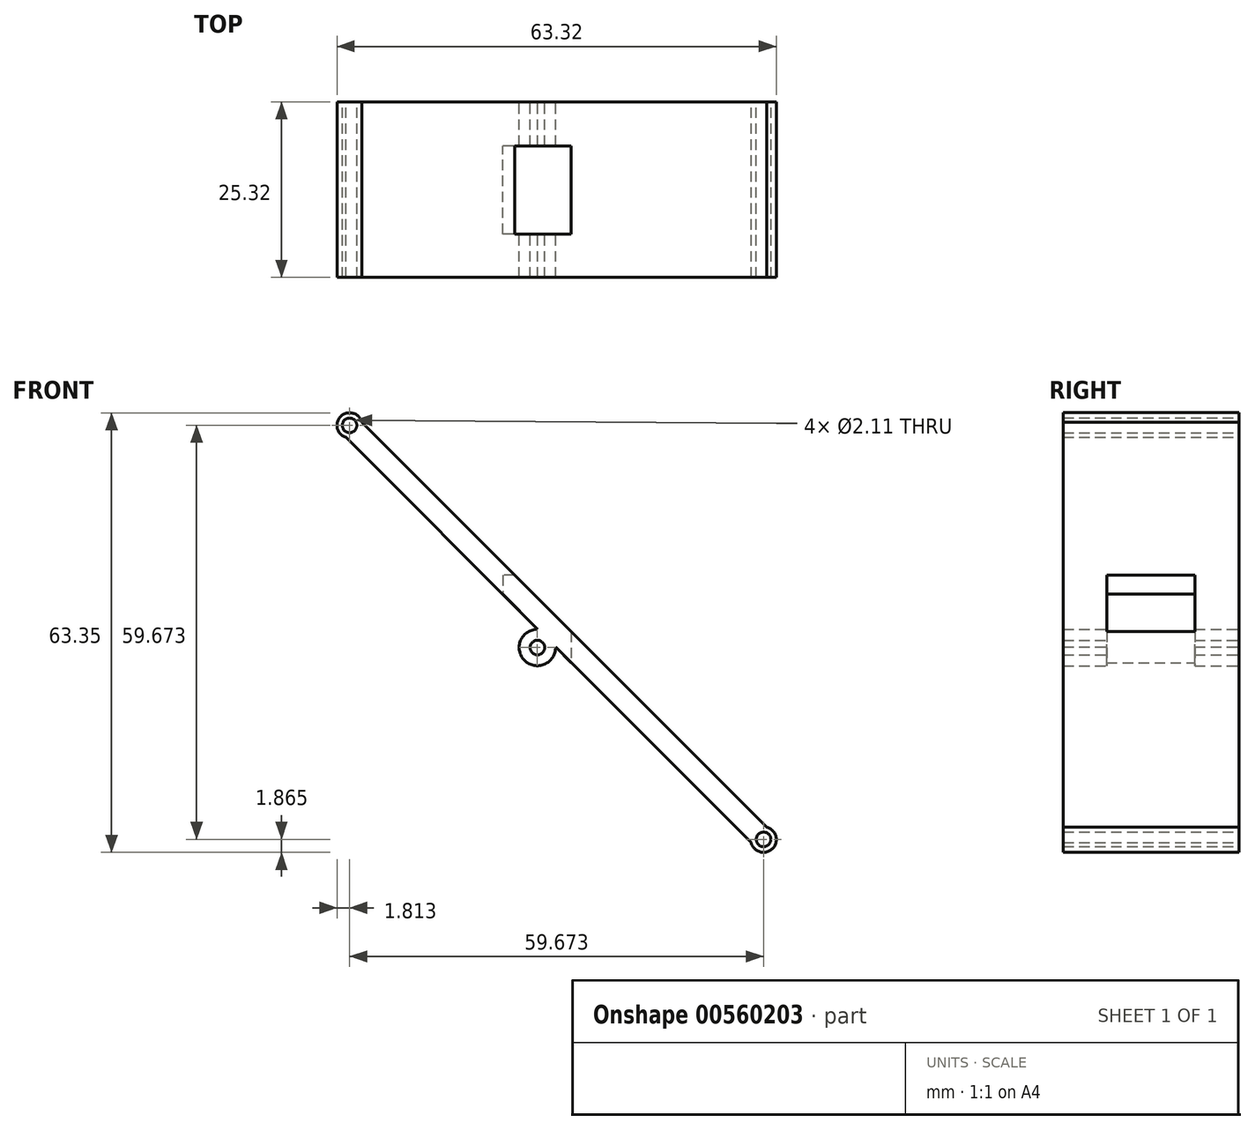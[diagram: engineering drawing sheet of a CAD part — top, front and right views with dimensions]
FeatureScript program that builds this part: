
annotation { "Feature Type Name" : "Feature", "Feature Type Description" : "" }
export const myFeature = defineFeature(function(context is Context, id is Id, definition is map)
    precondition{}
    {
        {
            var Q0;
            Q0=qCreatedBy(makeId("Front.planeOp"),FACE);
            var sketch = newSketch(context, id + "F0", { "sketchPlane" : qUnion([Q0])});
            skLineSegment(sketch, "E0", {"start": v(0, 0) * mm, "end": v(-9.73, 0) * mm, "construction": true});
            skArc(sketch, "E1", {"start": v(-1.78, -0.46) * mm, "mid": v(1.3, -1.3) * mm, "end": v(0.46, 1.78) * mm});
            skLineSegment(sketch, "E2.0", {"start": v(0.46, 1.78) * mm, "end": v(-57.9, 60.15) * mm});
            skLineSegment(sketch, "E3.0", {"start": v(-1.78, -0.46) * mm, "end": v(-29.98, 27.73) * mm});
            skArc(sketch, "E4.MirrorC", {"start": v(-60.2, 57.96) * mm, "mid": v(-60.92, 61.01) * mm, "end": v(-57.9, 60.15) * mm});
            skPoint(sketch, "E5.start.orphan", {"position": v(-30.97, 28.72) * mm});
            skCircle(sketch, "E6.0", {"center": v(-59.67, 59.7) * mm, "radius": 1.05 * mm});
            skCircle(sketch, "E7.MirrorC", {"center": v(0, 0.02) * mm, "radius": 1.05 * mm});
            skPoint(sketch, "E8.orphan", {"position": v(-60.15, 57.9) * mm});
            skArc(sketch, "E9", {"start": v(-32.54, 30.3) * mm, "mid": v(-34.45, 25.82) * mm, "end": v(-29.98, 27.73) * mm});
            skCircle(sketch, "E10.0", {"center": v(-32.6, 27.68) * mm, "radius": 1.05 * mm});
            skLineSegment(sketch, "E11.trimOffspring", {"start": v(-32.54, 30.3) * mm, "end": v(-60.2, 57.96) * mm});
            skSolve(sketch);
        }
        {
            var Q0;
            Q0=makeQuery(id+"F0.imprint","IMPRINT",FACE,{"disambiguationData":[TD([[makeQuery(id+"F0.imprint","IMPRINT",EDGE,{"derivedFrom":sQuery(id+"F0.wireOp",EDGE,"E1")}),1.0]])]});
            extrude(context, id + "F1", {"entities" : qUnion([Q0]), "depth" : 25.32 * mm, "offsetDistance" : 25.4 * mm});
        }
        {
            var Q0;
            Q0=qCreatedBy(makeId("Top.planeOp"),FACE);
            var sketch = newSketch(context, id + "F2", { "sketchPlane" : qUnion([Q0])});
            skLineSegment(sketch, "E12.bottom", {"start": v(-27.7, -19.05) * mm, "end": v(-37.6, -19.05) * mm});
            skLineSegment(sketch, "E12.top", {"start": v(-27.7, -6.35) * mm, "end": v(-37.6, -6.35) * mm});
            skLineSegment(sketch, "E12.left", {"start": v(-27.7, -19.05) * mm, "end": v(-27.7, -6.35) * mm});
            skLineSegment(sketch, "E12.right", {"start": v(-37.6, -19.05) * mm, "end": v(-37.6, -6.35) * mm});
            skSolve(sketch);
        }
        {
            var Q0;
            Q0 = qSketchRegion(id + "F2", true);
            extrude(context, id + "F3", {"entities" : qUnion([Q0]), "operationType" : NewBodyOperationType.REMOVE, "depth" : 38.1 * mm, "offsetDistance" : 25.4 * mm});
        }
        {
            var Q0;
            Q0=makeQuery(id+"F1.opExtrude","SWEPT_FACE",FACE,{"disambiguationData":[OSD([sQuery(id+"F0.wireOp",EDGE,"E2.0")])]});
            var sketch = newSketch(context, id + "F4", { "sketchPlane" : qUnion([Q0])});
            skLineSegment(sketch, "E13.bottom", {"start": v(-40.77, -19.05) * mm, "end": v(-3.75, -19.05) * mm});
            skLineSegment(sketch, "E13.top", {"start": v(-40.77, -6.35) * mm, "end": v(-3.75, -6.35) * mm});
            skLineSegment(sketch, "E13.left", {"start": v(-40.77, -19.05) * mm, "end": v(-40.77, -6.35) * mm});
            skLineSegment(sketch, "E13.right", {"start": v(-3.75, -19.05) * mm, "end": v(-3.75, -6.35) * mm});
            skSolve(sketch);
        }
        {
            var Q0;
            Q0 = qSketchRegion(id + "F4", true);
            extrude(context, id + "F5", {"entities" : qUnion([Q0]), "operationType" : NewBodyOperationType.REMOVE, "oppositeDirection" : true, "depth" : 25.4 * mm, "offsetDistance" : 25.4 * mm});
        }
    });
